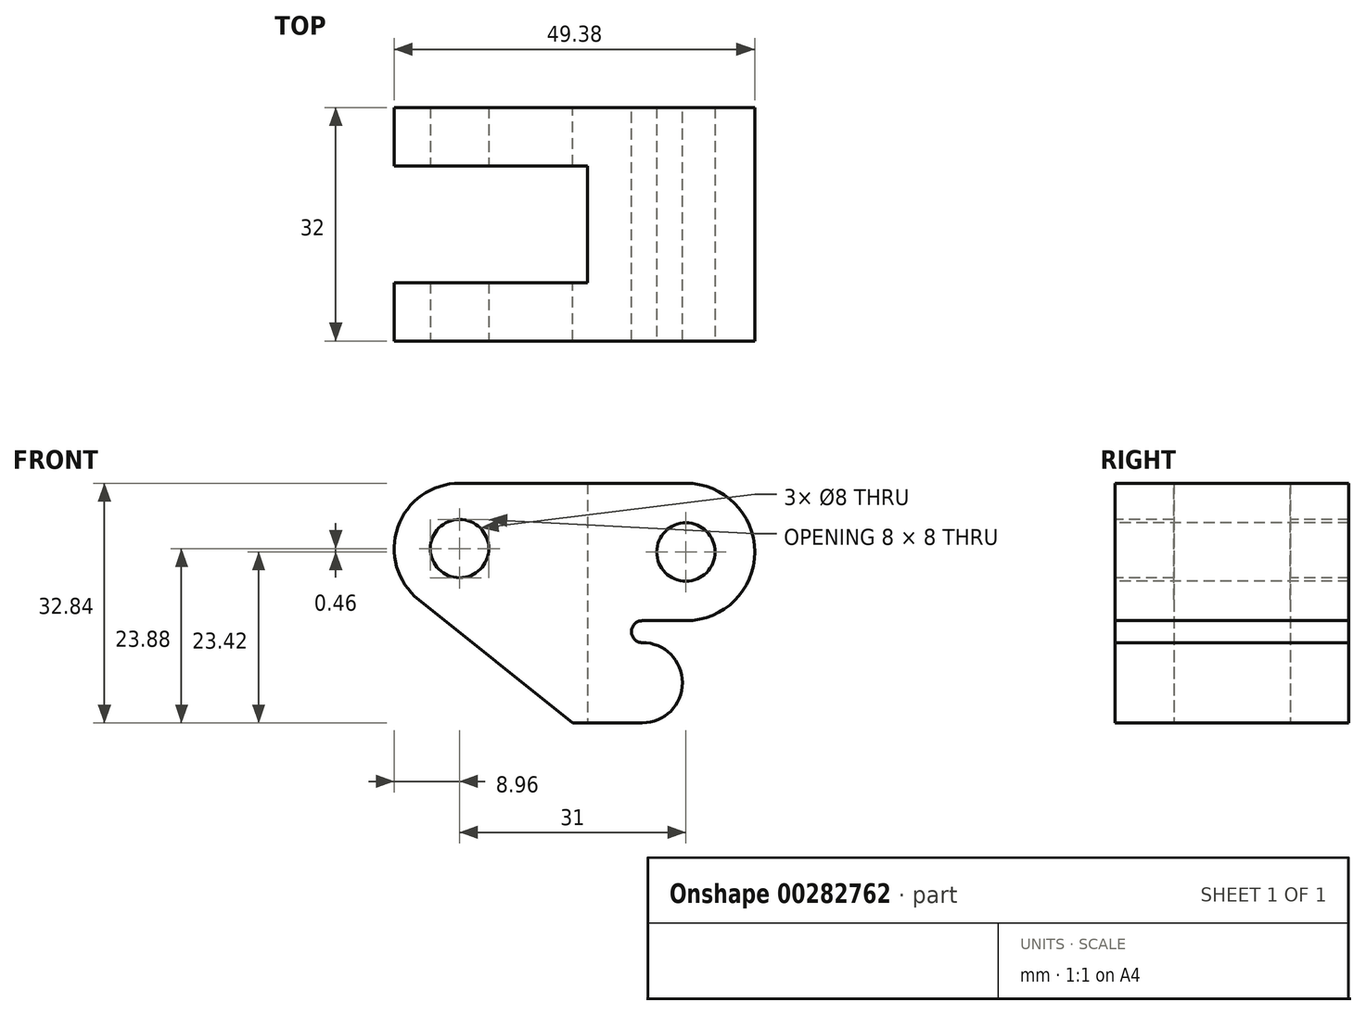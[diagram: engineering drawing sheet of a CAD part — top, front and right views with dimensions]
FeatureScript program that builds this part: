
annotation { "Feature Type Name" : "Feature", "Feature Type Description" : "" }
export const myFeature = defineFeature(function(context is Context, id is Id, definition is map)
    precondition{}
    {
        {
            var Q0;
            Q0=qCreatedBy(makeId("Front.planeOp"),FACE);
            var sketch = newSketch(context, id + "F0", { "sketchPlane" : qUnion([Q0])});
            skLineSegment(sketch, "E0", {"start": v(0, 0) * mm, "end": v(31, 0) * mm});
            skArc(sketch, "E1", {"start": v(31, -18.84) * mm, "mid": v(40.42, -9.42) * mm, "end": v(31, 0) * mm});
            skLineSegment(sketch, "E2", {"start": v(31, -18.84) * mm, "end": v(25.04, -18.84) * mm});
            skArc(sketch, "E3", {"start": v(25.04, -18.84) * mm, "mid": v(23.54, -20.34) * mm, "end": v(25.04, -21.84) * mm});
            skArc(sketch, "E4", {"start": v(25.04, -32.84) * mm, "mid": v(30.54, -27.34) * mm, "end": v(25.04, -21.84) * mm});
            skLineSegment(sketch, "E5", {"start": v(25.04, -32.84) * mm, "end": v(15.52, -32.84) * mm});
            skLineSegment(sketch, "E6", {"start": v(15.52, -32.84) * mm, "end": v(-5.6, -15.96) * mm});
            skArc(sketch, "E7", {"start": v(0, 0) * mm, "mid": v(-8.45, -6) * mm, "end": v(-5.6, -15.96) * mm});
            skCircle(sketch, "E8", {"center": v(0, -8.96) * mm, "radius": 4 * mm, "construction": true});
            skCircle(sketch, "E9", {"center": v(31, -9.42) * mm, "radius": 4 * mm, "construction": true});
            skSolve(sketch);
        }
        {
            var Q0;
            Q0 = qSketchRegion(id + "F0", true);
            extrude(context, id + "F1", {"entities" : qUnion([Q0]), "endBound" : BoundingType.SYMMETRIC, "depth" : 32 * mm});
        }
        {
            var Q0;
            Q0=makeQuery(id+"F1.opExtrude","SWEPT_FACE",FACE,{"disambiguationData":[OSD([sQuery(id+"F0.wireOp",EDGE,"E5")])]});
            var sketch = newSketch(context, id + "F2", { "sketchPlane" : qUnion([Q0])});
            skLineSegment(sketch, "E10.0", {"start": v(15.52, 16) * mm, "end": v(15.52, -16) * mm, "construction": true});
            skPoint(sketch, "E11", {"position": v(-5.6, 0) * mm});
            skLineSegment(sketch, "E12.bottom", {"start": v(-8.96, 8) * mm, "end": v(17.52, 8) * mm});
            skLineSegment(sketch, "E12.top", {"start": v(-8.96, -8) * mm, "end": v(17.52, -8) * mm});
            skLineSegment(sketch, "E12.left", {"start": v(-8.96, 8) * mm, "end": v(-8.96, -8) * mm});
            skLineSegment(sketch, "E12.right", {"start": v(17.52, 8) * mm, "end": v(17.52, -8) * mm});
            skLineSegment(sketch, "E13", {"start": v(-5.6, 0) * mm, "end": v(15.52, 0) * mm, "construction": true});
            skLineSegment(sketch, "E14", {"start": v(-8.96, -16) * mm, "end": v(-8.96, 16) * mm, "construction": true});
            skSolve(sketch);
        }
        {
            var Q0;
            Q0 = qSketchRegion(id + "F2", true);
            extrude(context, id + "F3", {"entities" : qUnion([Q0]), "operationType" : NewBodyOperationType.REMOVE, "endBound" : BoundingType.THROUGH_ALL, "oppositeDirection" : true, "depth" : 25 * mm});
        }
        {
            var Q0;
            Q0=makeQuery(id+"F1.opExtrude","CAP_FACE",FACE,{"disambiguationData":[OSD([sQuery(id+"F0.wireOp",EDGE,"E0"),sQuery(id+"F0.wireOp",EDGE,"E1"),sQuery(id+"F0.wireOp",EDGE,"E2"),sQuery(id+"F0.wireOp",EDGE,"E3"),sQuery(id+"F0.wireOp",EDGE,"E4"),sQuery(id+"F0.wireOp",EDGE,"E5"),sQuery(id+"F0.wireOp",EDGE,"E6"),sQuery(id+"F0.wireOp",EDGE,"E7")])],"isStart":false});
            var sketch = newSketch(context, id + "F4", { "sketchPlane" : qUnion([Q0])});
            skArc(sketch, "E15.0", {"start": v(0, 0) * mm, "mid": v(-8.45, -6) * mm, "end": v(-5.6, -15.96) * mm, "construction": true});
            skArc(sketch, "E16.0", {"start": v(31, -18.84) * mm, "mid": v(40.42, -9.42) * mm, "end": v(31, 0) * mm, "construction": true});
            skSolve(sketch);
        }
        {
            var Q0;
            Q0=sQuery(id+"F4.wireOp",VERTEX,"E15.0.center");
            var Q1;
            Q1=sQuery(id+"F4.wireOp",VERTEX,"E16.0.center");
            var Q2;
            Q2=makeQuery(id+"F1.opExtrude","SWEPT_BODY",BODY,{"disambiguationData":[OSD([sQuery(id+"F0.wireOp",EDGE,"E0"),sQuery(id+"F0.wireOp",EDGE,"E1"),sQuery(id+"F0.wireOp",EDGE,"E2"),sQuery(id+"F0.wireOp",EDGE,"E3"),sQuery(id+"F0.wireOp",EDGE,"E4"),sQuery(id+"F0.wireOp",EDGE,"E5"),sQuery(id+"F0.wireOp",EDGE,"E6"),sQuery(id+"F0.wireOp",EDGE,"E7")])]});
            hole(context, id + "F5", {"style" : HoleStyle.SIMPLE, "endStyle" : HoleEndStyle.THROUGH, "holeDiameter" : 8 * mm, "tappedDepth" : 12 * mm, "tapClearance" : 3, "locations" : qUnion([Q0, Q1]), "scope" : qUnion([Q2])});
        }
    });
